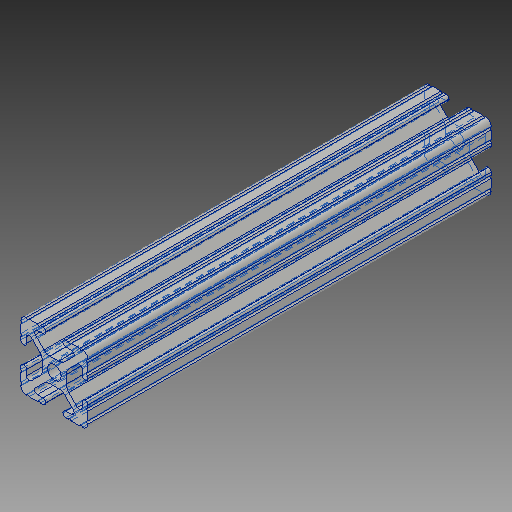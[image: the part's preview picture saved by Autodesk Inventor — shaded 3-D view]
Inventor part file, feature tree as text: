
AUTODESK INVENTOR PART (.ipt)
format: ipt  version: 2019 (Build 230136000, 136)  size: 343,040 bytes
history: native  units: in
note: dims shown in document units (in); Inventor stores cm internally (conversion verified against a paired STEP export)
features: other x1, extrude x1, sketch x1, projected_geometry x1
ambient origin geometry x8: Origin, YZ Plane, XZ Plane, XY Plane, X Axis, Y Axis, Z Axis, Center Point
bodies: Solid1 (feature_tree)
feature tree (4):
  other  "Boss-Extrude1"
  extrude  "Extrusion2"  [1 undecoded]
  sketch  "Sketch2"  dims[d2=6.0in d3=0.0in]
  projected_geometry  "Projected Loop2"
note: 1 required parameter value undecoded (feature->parameter linkage not recoverable at this tier; creation-order binding heuristic only, values carry confidence <= 0.55)
